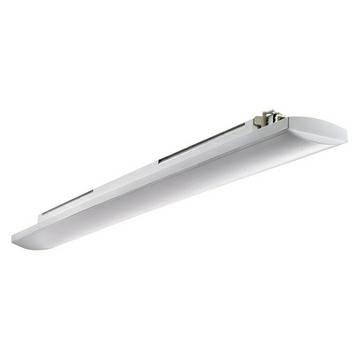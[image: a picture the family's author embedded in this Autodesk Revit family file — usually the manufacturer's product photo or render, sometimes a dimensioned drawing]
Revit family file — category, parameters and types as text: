
# Revit family: Lighting-Industriale-GEWISS-SMART[3]PLUS-HLO-PLAFONIERA-LED-EMERGENZA_OPALE_1600mm
name_source: partatom
category: Apparecchi per illuminazione
units: mm (PartAtom-declared; Revit-internal decimal feet)

## family parameters
Condiviso = No
Host = Superficie
Numero OmniClass = 23.80.70.11
Punto di calcolo locali = No
Quota connettore circolare = Usa diametro
Sorgente d'illuminazione = No
Taglio con vuoti quando caricato = No
Tipo di parte = Normale
Titolo OmniClass = Luminaries for Internal Lighting

## types (1)
- Lighting-Industriale-GEWISS-SMART[3]PLUS-HLO-PLAFONIERA-LED-EMERGENZA_OPALE_1600mm
    Applicazione = Interno
    Carico apparente = 27 VA
    Catalogo = LIGHTING
    Catalogo Serie = SMART[3] PLUS HLO
    Classe di efficienza LED integrati = A ÷ A++
    Classe isolamento = II
    Codice Electrocod = 2434
    Commenti sul wattaggio = 27W
    Descrizione = SMART3 PLUS 1600 EMERG DT1+DT6 HO OPAL 9 57
    Ganci = GEWISS  - ALLUMINIO
    Garanzia = ND
    Glow Wire Test = 850°C
    Grado di protezione = IP66/IP69
    IDF = 02c8b766-df71-47cb-9ea1-76a434de284a
    IDT = 42ad88ef-a339-4291-a014-784caecbcb9b
    Immagine tipo = GWS3158P.jpg
    Lampada = LED
    Lampada: = LED
    Lumen output (lm) = 6600
    Lunghezza = 1600 mm
    Lunghezza Lampada = 1600 mm  [stored 5.24934 ft]
    Modello = GWS3325BP957
    Potenza di sistema = 50 W
    Produttore = GEWISS S.p.A.
    Prospetto di default = 1219 mm
    Resistenza agli urti = IK08
    SEO = Plafoniera
    Scheda Tecnica = https://www.gewiss.com
    Schermo = Opale
    Schermo. = Gewiss - Led Acceso
    Stampa 1_100 = Sì
    Stampa 1_200 = No
    Struttura = GEWISS - SMART 3 - GRIGIO
    Temperatura di colore = 5700 K (CRI > 90)
    Temperatura di colore: = 5700 K (CRI > 90)
    Temperatura di funzionamento = ND
    Temperatura di utilizzo = ND
    Tensione = 220-240 V
    Tipologia sorgente luminosa = LED - Non sostituibile
    URL = https://www.gewiss.com
    Versione file RFA = 20.0

note: [stored X ft] marks values corroborated as IEEE doubles in the binary element streams (Revit-internal decimal feet)
